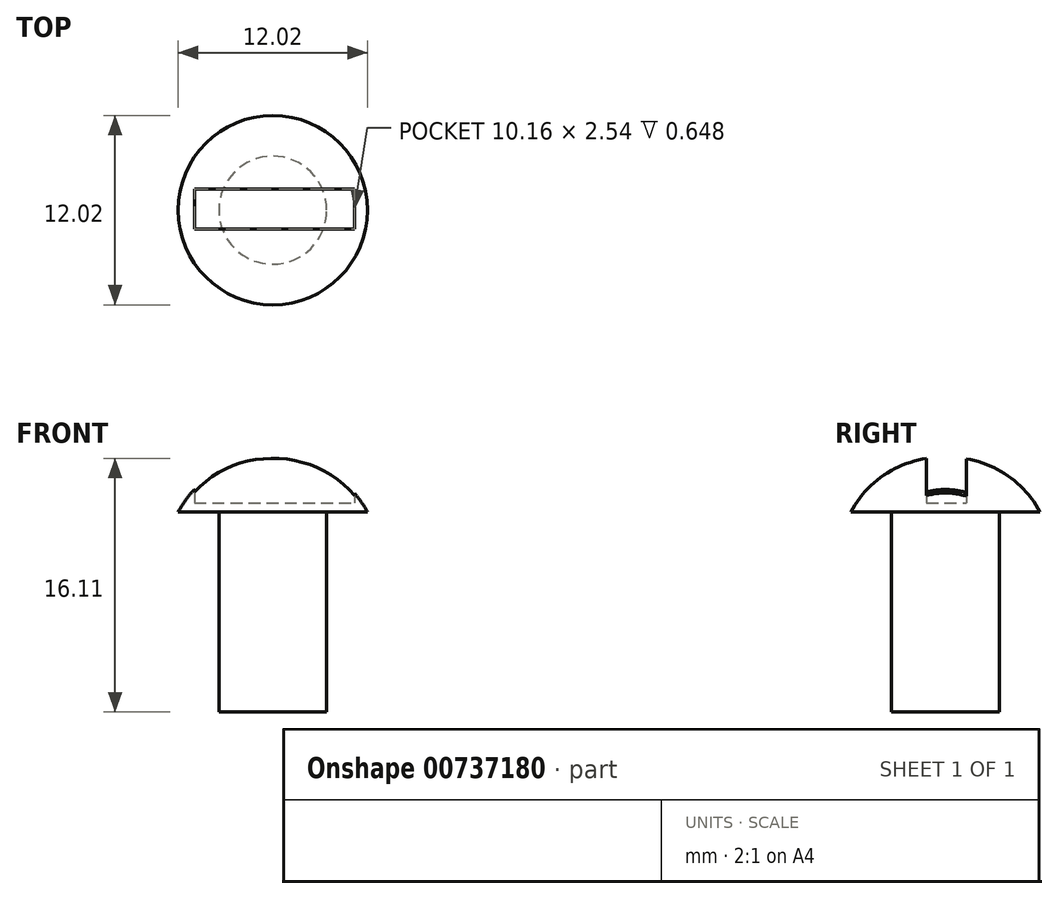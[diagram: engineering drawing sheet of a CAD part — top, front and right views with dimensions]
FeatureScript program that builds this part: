
annotation { "Feature Type Name" : "Feature", "Feature Type Description" : "" }
export const myFeature = defineFeature(function(context is Context, id is Id, definition is map)
    precondition{}
    {
        {
            var Q0;
            Q0=qCreatedBy(makeId("Front.planeOp"),FACE);
            var sketch = newSketch(context, id + "F0", { "sketchPlane" : qUnion([Q0])});
            skLineSegment(sketch, "E0", {"start": v(0, -6.91) * mm, "end": v(0, 9.27) * mm});
            skLineSegment(sketch, "E1", {"start": v(0, -6.91) * mm, "end": v(3.43, -6.91) * mm});
            skLineSegment(sketch, "E2", {"start": v(3.43, -6.91) * mm, "end": v(3.43, 5.79) * mm});
            skLineSegment(sketch, "E3", {"start": v(3.43, 5.79) * mm, "end": v(6.01, 5.79) * mm});
            skArc(sketch, "E4", {"start": v(6.01, 5.79) * mm, "mid": v(3.5, 8.38) * mm, "end": v(0, 9.27) * mm});
            skSolve(sketch);
        }
        {
            var Q0;
            Q0 = qSketchRegion(id + "F0", true);
            var Q1;
            Q1=sQuery(id+"F0.wireOp",EDGE,"E0");
            revolve(context, id + "F1", {"surfaceOperationType" : NewSurfaceOperationType.NEW, "entities" : qUnion([Q0]), "axis" : qUnion([Q1]), "revolveType" : RevolveType.FULL});
        }
        {
            var Q0;
            Q0=qCreatedBy(makeId("Top.planeOp"),FACE);
            cPlane(context, id + "F2", {"entities" : qUnion([Q0]), "cplaneType" : CPlaneType.OFFSET, "offset" : 6.35 * mm, "width" : 152.4 * mm, "height" : 152.4 * mm});
        }
        {
            var Q0;
            Q0=qCreatedBy(id+"F2.planeOp",FACE);
            var sketch = newSketch(context, id + "F3", { "sketchPlane" : qUnion([Q0])});
            skLineSegment(sketch, "E5.bottom", {"start": v(-4.98, -1.2) * mm, "end": v(5.18, -1.2) * mm});
            skLineSegment(sketch, "E5.top", {"start": v(-4.98, 1.34) * mm, "end": v(5.18, 1.34) * mm});
            skLineSegment(sketch, "E5.left", {"start": v(-4.98, -1.2) * mm, "end": v(-4.98, 1.34) * mm});
            skLineSegment(sketch, "E5.right", {"start": v(5.18, -1.2) * mm, "end": v(5.18, 1.34) * mm});
            skSolve(sketch);
        }
        {
            var Q0;
            Q0 = qSketchRegion(id + "F3", true);
            extrude(context, id + "F4", {"entities" : qUnion([Q0]), "operationType" : NewBodyOperationType.REMOVE, "depth" : 25.4 * mm, "offsetDistance" : 25.4 * mm});
        }
    });
